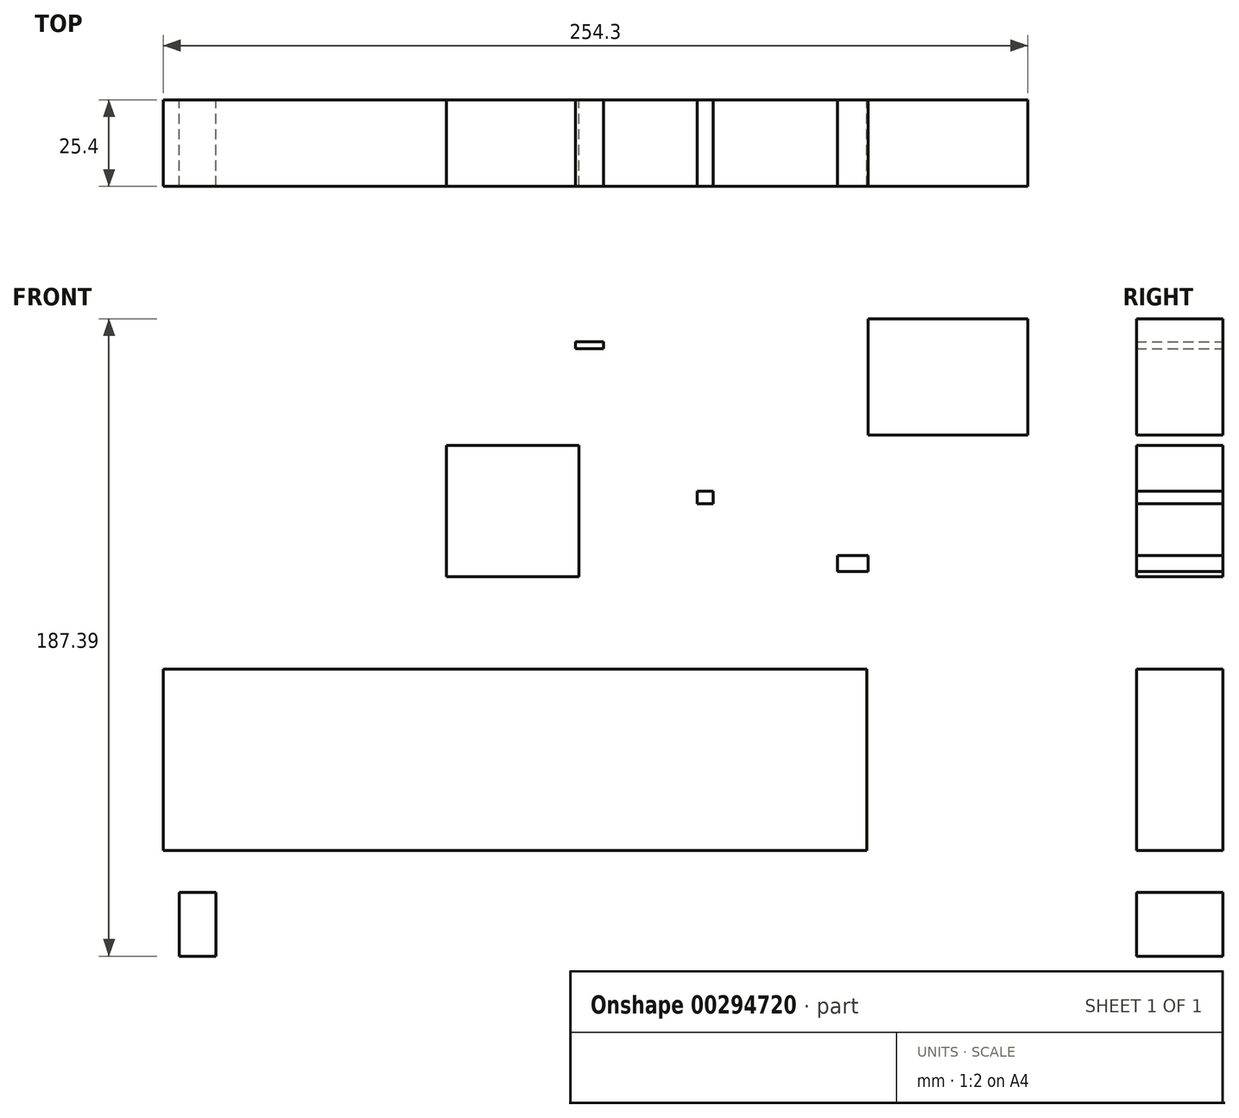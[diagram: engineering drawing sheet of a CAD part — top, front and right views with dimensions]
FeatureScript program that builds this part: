
annotation { "Feature Type Name" : "Feature", "Feature Type Description" : "" }
export const myFeature = defineFeature(function(context is Context, id is Id, definition is map)
    precondition{}
    {
        {
            var Q0;
            Q0=qCreatedBy(makeId("Front.planeOp"),FACE);
            var sketch = newSketch(context, id + "F0", { "sketchPlane" : qUnion([Q0])});
            skLineSegment(sketch, "E0.bottom", {"start": v(-82.85, 77.23) * mm, "end": v(-43.76, 77.23) * mm});
            skLineSegment(sketch, "E0.top", {"start": v(-82.85, 38.66) * mm, "end": v(-43.76, 38.66) * mm});
            skLineSegment(sketch, "E0.left", {"start": v(-82.85, 77.23) * mm, "end": v(-82.85, 38.66) * mm});
            skLineSegment(sketch, "E0.right", {"start": v(-43.76, 77.23) * mm, "end": v(-43.76, 38.66) * mm});
            skLineSegment(sketch, "E1.bottom", {"start": v(-8.97, 63.77) * mm, "end": v(-4.3, 63.77) * mm});
            skLineSegment(sketch, "E1.top", {"start": v(-8.97, 60.1) * mm, "end": v(-4.3, 60.1) * mm});
            skLineSegment(sketch, "E1.left", {"start": v(-8.97, 63.77) * mm, "end": v(-8.97, 60.1) * mm});
            skLineSegment(sketch, "E1.right", {"start": v(-4.3, 63.77) * mm, "end": v(-4.3, 60.1) * mm});
            skLineSegment(sketch, "E2.bottom", {"start": v(40.89, 11.44) * mm, "end": v(-166.07, 11.44) * mm});
            skLineSegment(sketch, "E2.top", {"start": v(40.89, -41.84) * mm, "end": v(-166.07, -41.84) * mm});
            skLineSegment(sketch, "E2.left", {"start": v(40.89, 11.44) * mm, "end": v(40.89, -41.84) * mm});
            skLineSegment(sketch, "E2.right", {"start": v(-166.07, 11.44) * mm, "end": v(-166.07, -41.84) * mm});
            skLineSegment(sketch, "E3.bottom", {"start": v(-161.4, -54.13) * mm, "end": v(-150.64, -54.13) * mm});
            skLineSegment(sketch, "E3.top", {"start": v(-161.4, -72.9) * mm, "end": v(-150.64, -72.9) * mm});
            skLineSegment(sketch, "E3.left", {"start": v(-161.4, -54.13) * mm, "end": v(-161.4, -72.9) * mm});
            skLineSegment(sketch, "E3.right", {"start": v(-150.64, -54.13) * mm, "end": v(-150.64, -72.9) * mm});
            skLineSegment(sketch, "E4.bottom", {"start": v(32.28, 40.16) * mm, "end": v(41.25, 40.16) * mm});
            skLineSegment(sketch, "E4.top", {"start": v(32.28, 44.9) * mm, "end": v(41.25, 44.9) * mm});
            skLineSegment(sketch, "E4.left", {"start": v(32.28, 40.16) * mm, "end": v(32.28, 44.9) * mm});
            skLineSegment(sketch, "E4.right", {"start": v(41.25, 40.16) * mm, "end": v(41.25, 44.9) * mm});
            skLineSegment(sketch, "E5.bottom", {"start": v(88.23, 80.35) * mm, "end": v(41.25, 80.35) * mm});
            skLineSegment(sketch, "E5.top", {"start": v(88.23, 114.49) * mm, "end": v(41.25, 114.49) * mm});
            skLineSegment(sketch, "E5.left", {"start": v(88.23, 80.35) * mm, "end": v(88.23, 114.49) * mm});
            skLineSegment(sketch, "E5.right", {"start": v(41.25, 80.35) * mm, "end": v(41.25, 114.49) * mm});
            skLineSegment(sketch, "E6.bottom", {"start": v(-36.58, 107.8) * mm, "end": v(-44.83, 107.8) * mm});
            skLineSegment(sketch, "E6.top", {"start": v(-36.58, 105.78) * mm, "end": v(-44.83, 105.78) * mm});
            skLineSegment(sketch, "E6.left", {"start": v(-36.58, 107.8) * mm, "end": v(-36.58, 105.78) * mm});
            skLineSegment(sketch, "E6.right", {"start": v(-44.83, 107.8) * mm, "end": v(-44.83, 105.78) * mm});
            skSolve(sketch);
        }
        {
            var Q0;
            Q0 = qSketchRegion(id + "F0", true);
            extrude(context, id + "F1", {"entities" : qUnion([Q0]), "depth" : 25.4 * mm});
        }
    });
